# Revit family: 7911 Sabina 280 LED
name_source: partatom
category: Lighting Fixtures
revit_build: Autodesk Revit 2017 (Build: 20160225_1515(x64)
units: mm (PartAtom-declared; Revit-internal decimal feet)

## family parameters
Always vertical = Yes
Cut with Voids When Loaded = No
Host = Wall
Light Source = Yes
OmniClass Number = 23.80.70.00
OmniClass Title = Lighting
Part Type = Normal
Room Calculation Point = No
Round Connector Dimension = Use Diameter
Shared = No

## types (2) — shared parameters
Color Filter = 16777215
Dimming Lamp Color Temperature Shift = <None>
Manufacturer = Astro Lighting Ltd
URL = www.astrolighting.com

## per-type parameters (varying)
| type | ADA compliant | Dimmable | Driver Included | Driver Required | Efficacy (lm/w) | Electrical Class | Emit from Line Length | Lamp | Light Source Fixed | Location rating | Main Finish | Main Material | Mounting Location | Photometric Web File | Power (Watts) | Product Code | Product Location | Product Name | Product SKU | Tilt Angle |
| CE |  | No | Yes | Yes | 59 | 2 | 1 mm  [stored 0.00328084 ft] | LED | Yes | IP44 | White Glass (Opal) | Glass | Ceiling only | TRN-18331  Sabina 280 LED 7911.ies | 15.8 | 7911 | Zone 2 and 3 | Sabina 280 LED | 1292007 | 0.00° |
| ETL | NO |  |  | No |  | 0 | 610 mm |  |  | DAMP |  | Metal - Steel |  | generic |  | 1234 | Bathroom |  | 1234001 | 60.00° |

note: [stored X ft] marks values corroborated as IEEE doubles in the binary element streams (Revit-internal decimal feet)

## geometry (parser evidence)
native form markers: Sweep x1
no freeform markers — native parametric forms only
